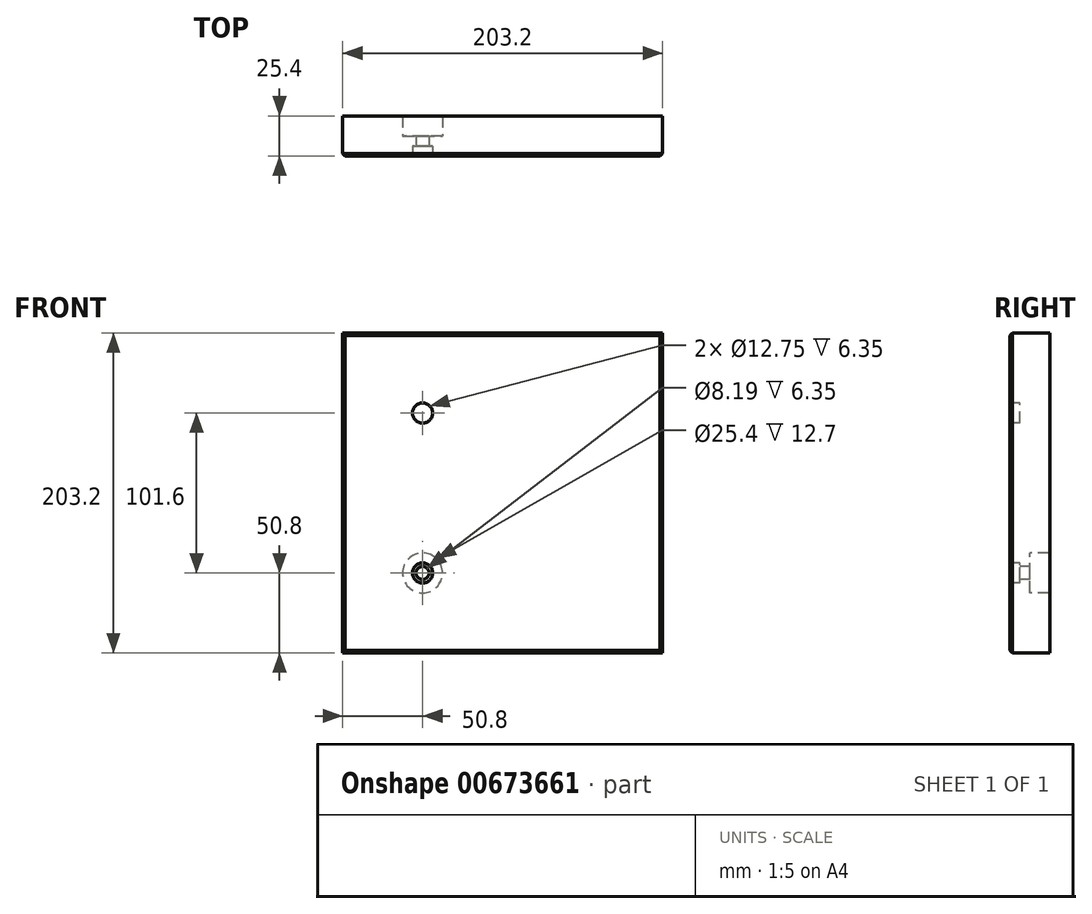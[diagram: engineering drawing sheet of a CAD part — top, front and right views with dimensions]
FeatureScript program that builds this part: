
annotation { "Feature Type Name" : "Feature", "Feature Type Description" : "" }
export const myFeature = defineFeature(function(context is Context, id is Id, definition is map)
    precondition{}
    {
        {
            var Q0;
            Q0=qCreatedBy(makeId("Front.planeOp"),FACE);
            var sketch = newSketch(context, id + "F0", { "sketchPlane" : qUnion([Q0])});
            skLineSegment(sketch, "E0.bottom", {"start": v(101.6, 101.6) * mm, "end": v(-101.6, 101.6) * mm});
            skLineSegment(sketch, "E0.top", {"start": v(101.6, -101.6) * mm, "end": v(-101.6, -101.6) * mm});
            skLineSegment(sketch, "E0.left", {"start": v(101.6, 101.6) * mm, "end": v(101.6, -101.6) * mm});
            skLineSegment(sketch, "E0.right", {"start": v(-101.6, 101.6) * mm, "end": v(-101.6, -101.6) * mm});
            skPoint(sketch, "E0.middle", {"position": v(0, 0) * mm});
            skSolve(sketch);
        }
        {
            var Q0;
            Q0 = qSketchRegion(id + "F0", true);
            extrude(context, id + "F1", {"entities" : qUnion([Q0]), "endBound" : BoundingType.SYMMETRIC, "depth" : 25.4 * mm, "offsetDistance" : 25.4 * mm});
        }
        {
            var Q0;
            Q0=makeQuery(id+"F1.opExtrude","CAP_FACE",FACE,{"disambiguationData":[OSD([sQuery(id+"F0.wireOp",EDGE,"E0.bottom"),sQuery(id+"F0.wireOp",EDGE,"E0.top"),sQuery(id+"F0.wireOp",EDGE,"E0.left"),sQuery(id+"F0.wireOp",EDGE,"E0.right")])],"isStart":false});
            chamfer(context, id + "F2", {"entities" : qUnion([Q0]), "width" : 1.52 * mm, "tangentPropagation" : true});
        }
        {
            var Q0;
            Q0=makeQuery(id+"F1.opExtrude","CAP_FACE",FACE,{"disambiguationData":[OSD([sQuery(id+"F0.wireOp",EDGE,"E0.bottom"),sQuery(id+"F0.wireOp",EDGE,"E0.top"),sQuery(id+"F0.wireOp",EDGE,"E0.left"),sQuery(id+"F0.wireOp",EDGE,"E0.right")])],"isStart":false});
            var sketch = newSketch(context, id + "F3", { "sketchPlane" : qUnion([Q0])});
            skCircle(sketch, "E1", {"center": v(-50.8, -50.8) * mm, "radius": 12.7 * mm});
            skSolve(sketch);
        }
        {
            var Q0;
            Q0=makeQuery(id+"F3.imprint","IMPRINT",FACE,{"disambiguationData":[TD([[makeQuery(id+"F3.imprint","IMPRINT",EDGE,{"derivedFrom":sQuery(id+"F3.wireOp",EDGE,"E1")}),1.0]])]});
            extrude(context, id + "F4", {"entities" : qUnion([Q0]), "operationType" : NewBodyOperationType.REMOVE, "endBound" : BoundingType.THROUGH_ALL, "oppositeDirection" : true, "depth" : 25.4 * mm, "offsetDistance" : 25.4 * mm});
        }
        {
            var Q0;
            Q0=makeQuery(id+"F1.opExtrude","CAP_FACE",FACE,{"disambiguationData":[OSD([sQuery(id+"F0.wireOp",EDGE,"E0.bottom"),sQuery(id+"F0.wireOp",EDGE,"E0.top"),sQuery(id+"F0.wireOp",EDGE,"E0.left"),sQuery(id+"F0.wireOp",EDGE,"E0.right")])],"isStart":false});
            var sketch = newSketch(context, id + "F5", { "sketchPlane" : qUnion([Q0])});
            skCircle(sketch, "E2", {"center": v(-50.8, 50.8) * mm, "radius": 12.7 * mm});
            skCircle(sketch, "E3", {"center": v(-50.8, 50.8) * mm, "radius": 4.1 * mm});
            skCircle(sketch, "E4", {"center": v(-50.8, -50.8) * mm, "radius": 4.1 * mm});
            skCircle(sketch, "E5", {"center": v(-50.8, -50.8) * mm, "radius": 12.7 * mm});
            skSolve(sketch);
        }
        {
            var Q0;
            Q0 = qSketchRegion(id + "F5", true);
            extrude(context, id + "F6", {"entities" : qUnion([Q0]), "operationType" : NewBodyOperationType.ADD, "oppositeDirection" : true, "depth" : 12.7 * mm, "offsetDistance" : 25.4 * mm});
        }
        {
            var Q0;
            Q0=makeQuery(id+"F6.boolean.opBoolean","MERGE",FACE,{"derivedFrom":[makeQuery(id+"F1.opExtrude","CAP_FACE",FACE,{"disambiguationData":[OSD([sQuery(id+"F0.wireOp",EDGE,"E0.bottom"),sQuery(id+"F0.wireOp",EDGE,"E0.top"),sQuery(id+"F0.wireOp",EDGE,"E0.left"),sQuery(id+"F0.wireOp",EDGE,"E0.right")])],"isStart":false}),makeQuery(id+"F6.opExtrude","CAP_FACE",FACE,{"disambiguationData":[OSD([sQuery(id+"F5.wireOp",EDGE,"E2"),sQuery(id+"F5.wireOp",EDGE,"E3")])],"isStart":true}),makeQuery(id+"F6.opExtrude","CAP_FACE",FACE,{"disambiguationData":[OSD([sQuery(id+"F5.wireOp",EDGE,"E4"),sQuery(id+"F5.wireOp",EDGE,"E5")])],"isStart":true})]});
            var sketch = newSketch(context, id + "F7", { "sketchPlane" : qUnion([Q0])});
            skCircle(sketch, "E6", {"center": v(-50.8, 50.8) * mm, "radius": 6.38 * mm});
            skCircle(sketch, "E7", {"center": v(-50.8, -50.8) * mm, "radius": 6.38 * mm});
            skSolve(sketch);
        }
        {
            var Q0;
            Q0 = qSketchRegion(id + "F7", true);
            extrude(context, id + "F8", {"entities" : qUnion([Q0]), "operationType" : NewBodyOperationType.REMOVE, "oppositeDirection" : true, "depth" : 6.35 * mm, "offsetDistance" : 25.4 * mm});
        }
    });
